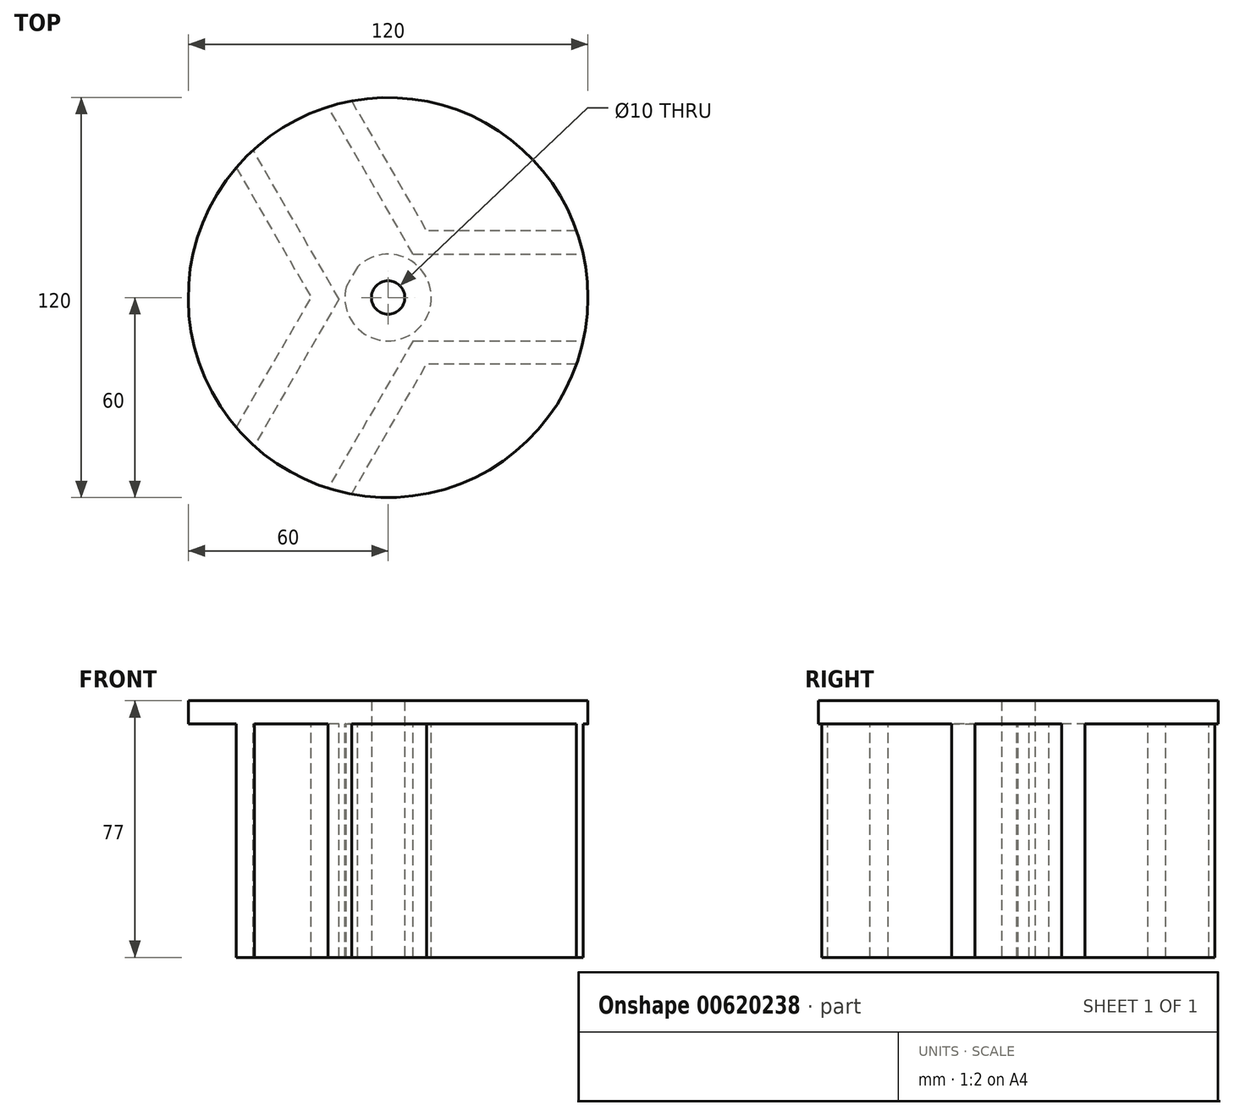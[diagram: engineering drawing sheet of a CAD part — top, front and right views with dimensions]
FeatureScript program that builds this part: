
annotation { "Feature Type Name" : "Feature", "Feature Type Description" : "" }
export const myFeature = defineFeature(function(context is Context, id is Id, definition is map)
    precondition{}
    {
        {
            var Q0;
            Q0=qCreatedBy(makeId("Top.planeOp"),FACE);
            var sketch = newSketch(context, id + "F0", { "sketchPlane" : qUnion([Q0])});
            skCircle(sketch, "E0", {"center": v(0, 0) * mm, "radius": 60 * mm});
            skCircle(sketch, "E1", {"center": v(0, 0) * mm, "radius": 5 * mm});
            skCircle(sketch, "E2", {"center": v(0, 0) * mm, "radius": 13 * mm});
            skLineSegment(sketch, "E3", {"start": v(0, 13) * mm, "end": v(58.57, 13) * mm});
            skLineSegment(sketch, "E4", {"start": v(0, -13) * mm, "end": v(58.57, -13) * mm});
            skLineSegment(sketch, "E5", {"start": v(11.26, 6.5) * mm, "end": v(-18.03, 57.23) * mm});
            skLineSegment(sketch, "E6", {"start": v(-11.46, -6.14) * mm, "end": v(-40.54, 44.23) * mm});
            skLineSegment(sketch, "E7", {"start": v(-9.12, 9.26) * mm, "end": v(-40.2, -44.55) * mm});
            skLineSegment(sketch, "E8", {"start": v(11.26, -6.5) * mm, "end": v(-18.03, -57.23) * mm});
            skLineSegment(sketch, "E9", {"start": v(-45.6, 39) * mm, "end": v(-18.78, -7.46) * mm});
            skLineSegment(sketch, "E10", {"start": v(-45.6, -39) * mm, "end": v(-23.09, 0) * mm});
            skLineSegment(sketch, "E11", {"start": v(-10.96, -58.99) * mm, "end": v(15.59, -13) * mm});
            skLineSegment(sketch, "E12", {"start": v(56.57, -20) * mm, "end": v(3.46, -20) * mm});
            skLineSegment(sketch, "E13", {"start": v(56.57, 20) * mm, "end": v(3.46, 20) * mm});
            skLineSegment(sketch, "E14", {"start": v(-10.96, 58.99) * mm, "end": v(15.59, 13) * mm});
            skSolve(sketch);
        }
        {
            var Q0;
            {var subQ0=sQuery(id+"F0.wireOp",EDGE,"E13");var subQ1=sQuery(id+"F0.wireOp",EDGE,"E0");var subQ2=makeQuery(id+"F0.imprint","INTERSECT",VERTEX,{"derivedFrom":[subQ1,subQ0]});Q0=makeQuery(id+"F0.imprint","IMPRINT",FACE,{"disambiguationData":[TD([[makeQuery(id+"F0.imprint","IMPRINT",EDGE,{"disambiguationData":[TD([[subQ2,-1.0]])],"derivedFrom":subQ1}),1.0]])]});}
            var Q1;
            {var subQ0=sQuery(id+"F0.wireOp",EDGE,"E11");var subQ1=sQuery(id+"F0.wireOp",EDGE,"E0");var subQ2=makeQuery(id+"F0.imprint","INTERSECT",VERTEX,{"derivedFrom":[subQ1,subQ0]});Q1=makeQuery(id+"F0.imprint","IMPRINT",FACE,{"disambiguationData":[TD([[makeQuery(id+"F0.imprint","IMPRINT",EDGE,{"disambiguationData":[TD([[subQ2,-1.0]])],"derivedFrom":subQ1}),1.0]])]});}
            var Q2;
            {var subQ0=sQuery(id+"F0.wireOp",EDGE,"E3");var subQ1=sQuery(id+"F0.wireOp",EDGE,"E0");var subQ2=makeQuery(id+"F0.imprint","INTERSECT",VERTEX,{"derivedFrom":[subQ1,subQ0]});Q2=makeQuery(id+"F0.imprint","IMPRINT",FACE,{"disambiguationData":[TD([[makeQuery(id+"F0.imprint","IMPRINT",EDGE,{"disambiguationData":[TD([[subQ2,1.0]])],"derivedFrom":subQ1}),1.0]])]});}
            var Q3;
            {var subQ0=sQuery(id+"F0.wireOp",EDGE,"E4");var subQ1=sQuery(id+"F0.wireOp",EDGE,"E0");var subQ2=makeQuery(id+"F0.imprint","INTERSECT",VERTEX,{"derivedFrom":[subQ1,subQ0]});Q3=makeQuery(id+"F0.imprint","IMPRINT",FACE,{"disambiguationData":[TD([[makeQuery(id+"F0.imprint","IMPRINT",EDGE,{"disambiguationData":[TD([[subQ2,1.0]])],"derivedFrom":subQ1}),1.0]])]});}
            var Q4;
            {var subQ0=sQuery(id+"F0.wireOp",EDGE,"E3");var subQ1=sQuery(id+"F0.wireOp",EDGE,"E0");var subQ2=makeQuery(id+"F0.imprint","INTERSECT",VERTEX,{"derivedFrom":[subQ1,subQ0]});Q4=makeQuery(id+"F0.imprint","IMPRINT",FACE,{"disambiguationData":[TD([[makeQuery(id+"F0.imprint","IMPRINT",EDGE,{"disambiguationData":[TD([[subQ2,-1.0]])],"derivedFrom":subQ1}),1.0]])]});}
            var Q5;
            {var subQ3=sQuery(id+"F0.wireOp",EDGE,"E7");var subQ5=sQuery(id+"F0.wireOp",EDGE,"E0");var subQ6=makeQuery(id+"F0.imprint","INTERSECT",VERTEX,{"derivedFrom":[subQ5,subQ3]});Q5=makeQuery(id+"F0.imprint","IMPRINT",FACE,{"disambiguationData":[TD([[makeQuery(id+"F0.imprint","IMPRINT",EDGE,{"disambiguationData":[TD([[subQ6,-1.0]])],"derivedFrom":subQ5}),1.0]])]});}
            var Q6;
            {var subQ1=sQuery(id+"F0.wireOp",EDGE,"E0");var subQ6=sQuery(id+"F0.wireOp",EDGE,"E6");var subQ8=makeQuery(id+"F0.imprint","INTERSECT",VERTEX,{"derivedFrom":[subQ1,subQ6]});Q6=makeQuery(id+"F0.imprint","IMPRINT",FACE,{"disambiguationData":[TD([[makeQuery(id+"F0.imprint","IMPRINT",EDGE,{"disambiguationData":[TD([[subQ8,-1.0]])],"derivedFrom":subQ1}),1.0]])]});}
            var Q7;
            {var subQ3=sQuery(id+"F0.wireOp",EDGE,"E5");var subQ8=sQuery(id+"F0.wireOp",EDGE,"E0");var subQ9=makeQuery(id+"F0.imprint","INTERSECT",VERTEX,{"derivedFrom":[subQ8,subQ3]});Q7=makeQuery(id+"F0.imprint","IMPRINT",FACE,{"disambiguationData":[TD([[makeQuery(id+"F0.imprint","IMPRINT",EDGE,{"disambiguationData":[TD([[subQ9,-1.0]])],"derivedFrom":subQ8}),1.0]])]});}
            var Q8;
            {var subQ3=sQuery(id+"F0.wireOp",EDGE,"E10");Q8=makeQuery(id+"F0.imprint","IMPRINT",FACE,{"disambiguationData":[TD([[makeQuery(id+"F0.imprint","IMPRINT",EDGE,{"derivedFrom":subQ3}),1.0]])]});}
            var Q9;
            {var subQ0=sQuery(id+"F0.wireOp",EDGE,"E5");var subQ1=sQuery(id+"F0.wireOp",EDGE,"E0");var subQ2=makeQuery(id+"F0.imprint","INTERSECT",VERTEX,{"derivedFrom":[subQ1,subQ0]});Q9=makeQuery(id+"F0.imprint","IMPRINT",FACE,{"disambiguationData":[TD([[makeQuery(id+"F0.imprint","IMPRINT",EDGE,{"disambiguationData":[TD([[subQ2,1.0]])],"derivedFrom":subQ1}),1.0]])]});}
            var Q10;
            {var subQ3=sQuery(id+"F0.wireOp",EDGE,"E10");Q10=makeQuery(id+"F0.imprint","IMPRINT",FACE,{"disambiguationData":[TD([[makeQuery(id+"F0.imprint","IMPRINT",EDGE,{"derivedFrom":subQ3}),-1.0]])]});}
            var Q11;
            {var subQ0=sQuery(id+"F0.wireOp",EDGE,"E8");var subQ1=sQuery(id+"F0.wireOp",EDGE,"E0");var subQ2=makeQuery(id+"F0.imprint","INTERSECT",VERTEX,{"derivedFrom":[subQ1,subQ0]});Q11=makeQuery(id+"F0.imprint","IMPRINT",FACE,{"disambiguationData":[TD([[makeQuery(id+"F0.imprint","IMPRINT",EDGE,{"disambiguationData":[TD([[subQ2,-1.0]])],"derivedFrom":subQ1}),1.0]])]});}
            var Q12;
            {var subQ0=sQuery(id+"F0.wireOp",EDGE,"E11");var subQ1=sQuery(id+"F0.wireOp",EDGE,"E4");var subQ2=makeQuery(id+"F0.imprint","INTERSECT",VERTEX,{"derivedFrom":[subQ1,subQ0]});Q12=makeQuery(id+"F0.imprint","IMPRINT",FACE,{"disambiguationData":[TD([[makeQuery(id+"F0.imprint","IMPRINT",EDGE,{"disambiguationData":[TD([[subQ2,1.0]])],"derivedFrom":subQ1}),-1.0]])]});}
            var Q13;
            {var subQ0=sQuery(id+"F0.wireOp",EDGE,"E14");var subQ1=sQuery(id+"F0.wireOp",EDGE,"E3");var subQ2=makeQuery(id+"F0.imprint","INTERSECT",VERTEX,{"derivedFrom":[subQ1,subQ0]});Q13=makeQuery(id+"F0.imprint","IMPRINT",FACE,{"disambiguationData":[TD([[makeQuery(id+"F0.imprint","IMPRINT",EDGE,{"disambiguationData":[TD([[subQ2,1.0]])],"derivedFrom":subQ1}),1.0]])]});}
            var Q14;
            {var subQ0=sQuery(id+"F0.wireOp",EDGE,"E4");var subQ1=sQuery(id+"F0.wireOp",EDGE,"E2");var subQ2=makeQuery(id+"F0.imprint","INTERSECT",VERTEX,{"derivedFrom":[subQ1,subQ0]});Q14=makeQuery(id+"F0.imprint","IMPRINT",FACE,{"disambiguationData":[TD([[makeQuery(id+"F0.imprint","IMPRINT",EDGE,{"disambiguationData":[TD([[subQ2,-1.0]])],"derivedFrom":subQ1}),-1.0]])]});}
            var Q15;
            {var subQ0=sQuery(id+"F0.wireOp",EDGE,"E7");var subQ1=sQuery(id+"F0.wireOp",EDGE,"E2");var subQ2=makeQuery(id+"F0.imprint","INTERSECT",VERTEX,{"disambiguationData":[OD(0.0)],"derivedFrom":[subQ1,subQ0]});Q15=makeQuery(id+"F0.imprint","IMPRINT",FACE,{"disambiguationData":[TD([[makeQuery(id+"F0.imprint","IMPRINT",EDGE,{"disambiguationData":[TD([[subQ2,-1.0]])],"derivedFrom":subQ1}),1.0]])]});}
            var Q16;
            {var subQ0=sQuery(id+"F0.wireOp",EDGE,"E3");var subQ1=sQuery(id+"F0.wireOp",EDGE,"E2");var subQ2=makeQuery(id+"F0.imprint","INTERSECT",VERTEX,{"derivedFrom":[subQ1,subQ0]});Q16=makeQuery(id+"F0.imprint","IMPRINT",FACE,{"disambiguationData":[TD([[makeQuery(id+"F0.imprint","IMPRINT",EDGE,{"disambiguationData":[TD([[subQ2,1.0]])],"derivedFrom":subQ1}),-1.0]])]});}
            var Q17;
            {var subQ0=sQuery(id+"F0.wireOp",EDGE,"E6");var subQ1=sQuery(id+"F0.wireOp",EDGE,"E2");var subQ2=makeQuery(id+"F0.imprint","INTERSECT",VERTEX,{"derivedFrom":[subQ1,subQ0]});Q17=makeQuery(id+"F0.imprint","IMPRINT",FACE,{"disambiguationData":[TD([[makeQuery(id+"F0.imprint","IMPRINT",EDGE,{"disambiguationData":[TD([[subQ2,1.0]])],"derivedFrom":subQ1}),-1.0]])]});}
            var Q18;
            Q18=makeQuery(id+"F0.imprint","IMPRINT",FACE,{"disambiguationData":[TD([[makeQuery(id+"F0.imprint","IMPRINT",EDGE,{"derivedFrom":sQuery(id+"F0.wireOp",EDGE,"E1")}),-1.0]])]});
            extrude(context, id + "F1", {"entities" : qUnion([Q0, Q1, Q2, Q3, Q4, Q5, Q6, Q7, Q8, Q9, Q10, Q11, Q12, Q13, Q14, Q15, Q16, Q17, Q18]), "depth" : 7 * mm, "offsetDistance" : 25 * mm});
        }
        {
            var Q0;
            {var subQ0=sQuery(id+"F0.wireOp",EDGE,"E4");var subQ1=sQuery(id+"F0.wireOp",EDGE,"E0");var subQ2=makeQuery(id+"F0.imprint","INTERSECT",VERTEX,{"derivedFrom":[subQ1,subQ0]});Q0=makeQuery(id+"F0.imprint","IMPRINT",FACE,{"disambiguationData":[TD([[makeQuery(id+"F0.imprint","IMPRINT",EDGE,{"disambiguationData":[TD([[subQ2,1.0]])],"derivedFrom":subQ1}),1.0]])]});}
            var Q1;
            {var subQ0=sQuery(id+"F0.wireOp",EDGE,"E11");var subQ1=sQuery(id+"F0.wireOp",EDGE,"E4");var subQ2=makeQuery(id+"F0.imprint","INTERSECT",VERTEX,{"derivedFrom":[subQ1,subQ0]});Q1=makeQuery(id+"F0.imprint","IMPRINT",FACE,{"disambiguationData":[TD([[makeQuery(id+"F0.imprint","IMPRINT",EDGE,{"disambiguationData":[TD([[subQ2,1.0]])],"derivedFrom":subQ1}),-1.0]])]});}
            var Q2;
            {var subQ0=sQuery(id+"F0.wireOp",EDGE,"E8");var subQ1=sQuery(id+"F0.wireOp",EDGE,"E0");var subQ2=makeQuery(id+"F0.imprint","INTERSECT",VERTEX,{"derivedFrom":[subQ1,subQ0]});Q2=makeQuery(id+"F0.imprint","IMPRINT",FACE,{"disambiguationData":[TD([[makeQuery(id+"F0.imprint","IMPRINT",EDGE,{"disambiguationData":[TD([[subQ2,-1.0]])],"derivedFrom":subQ1}),1.0]])]});}
            var Q3;
            {var subQ3=sQuery(id+"F0.wireOp",EDGE,"E10");Q3=makeQuery(id+"F0.imprint","IMPRINT",FACE,{"disambiguationData":[TD([[makeQuery(id+"F0.imprint","IMPRINT",EDGE,{"derivedFrom":subQ3}),-1.0]])]});}
            var Q4;
            {var subQ1=sQuery(id+"F0.wireOp",EDGE,"E0");var subQ6=sQuery(id+"F0.wireOp",EDGE,"E6");var subQ8=makeQuery(id+"F0.imprint","INTERSECT",VERTEX,{"derivedFrom":[subQ1,subQ6]});Q4=makeQuery(id+"F0.imprint","IMPRINT",FACE,{"disambiguationData":[TD([[makeQuery(id+"F0.imprint","IMPRINT",EDGE,{"disambiguationData":[TD([[subQ8,-1.0]])],"derivedFrom":subQ1}),1.0]])]});}
            var Q5;
            {var subQ0=sQuery(id+"F0.wireOp",EDGE,"E5");var subQ1=sQuery(id+"F0.wireOp",EDGE,"E0");var subQ2=makeQuery(id+"F0.imprint","INTERSECT",VERTEX,{"derivedFrom":[subQ1,subQ0]});Q5=makeQuery(id+"F0.imprint","IMPRINT",FACE,{"disambiguationData":[TD([[makeQuery(id+"F0.imprint","IMPRINT",EDGE,{"disambiguationData":[TD([[subQ2,1.0]])],"derivedFrom":subQ1}),1.0]])]});}
            var Q6;
            {var subQ0=sQuery(id+"F0.wireOp",EDGE,"E14");var subQ1=sQuery(id+"F0.wireOp",EDGE,"E3");var subQ2=makeQuery(id+"F0.imprint","INTERSECT",VERTEX,{"derivedFrom":[subQ1,subQ0]});Q6=makeQuery(id+"F0.imprint","IMPRINT",FACE,{"disambiguationData":[TD([[makeQuery(id+"F0.imprint","IMPRINT",EDGE,{"disambiguationData":[TD([[subQ2,1.0]])],"derivedFrom":subQ1}),1.0]])]});}
            var Q7;
            {var subQ0=sQuery(id+"F0.wireOp",EDGE,"E3");var subQ1=sQuery(id+"F0.wireOp",EDGE,"E0");var subQ2=makeQuery(id+"F0.imprint","INTERSECT",VERTEX,{"derivedFrom":[subQ1,subQ0]});Q7=makeQuery(id+"F0.imprint","IMPRINT",FACE,{"disambiguationData":[TD([[makeQuery(id+"F0.imprint","IMPRINT",EDGE,{"disambiguationData":[TD([[subQ2,-1.0]])],"derivedFrom":subQ1}),1.0]])]});}
            var Q8;
            Q8=makeQuery(id+"F0.imprint","IMPRINT",FACE,{"disambiguationData":[TD([[makeQuery(id+"F0.imprint","IMPRINT",EDGE,{"derivedFrom":sQuery(id+"F0.wireOp",EDGE,"E1")}),-1.0]])]});
            extrude(context, id + "F2", {"entities" : qUnion([Q0, Q1, Q2, Q3, Q4, Q5, Q6, Q7, Q8]), "operationType" : NewBodyOperationType.ADD, "oppositeDirection" : true, "depth" : 70 * mm, "offsetDistance" : 25 * mm});
        }
    });
